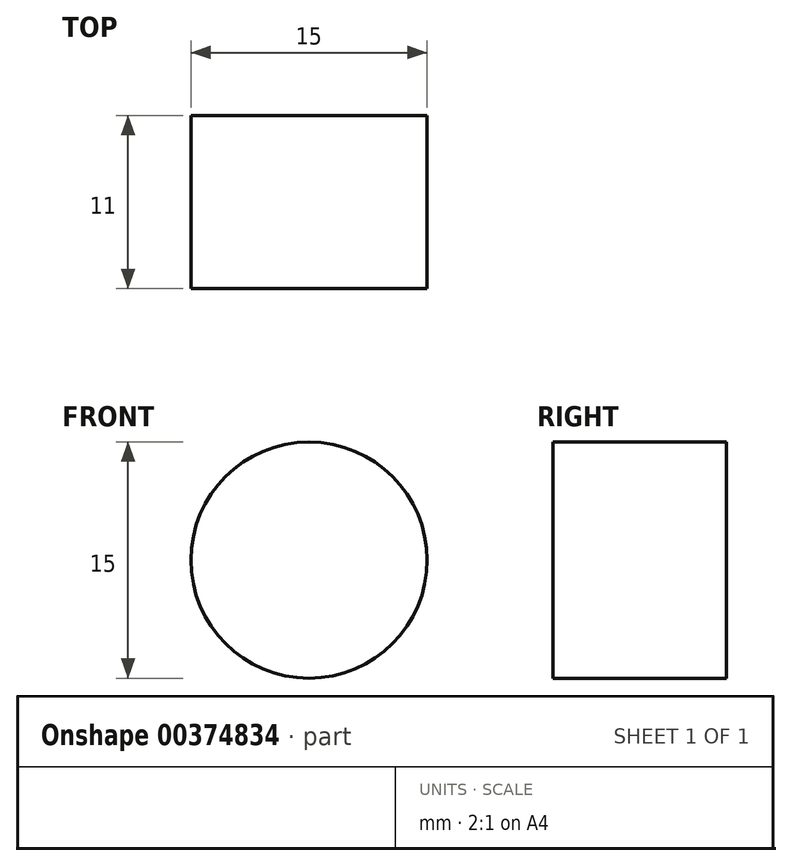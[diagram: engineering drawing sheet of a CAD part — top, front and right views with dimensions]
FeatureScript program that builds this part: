
annotation { "Feature Type Name" : "Feature", "Feature Type Description" : "" }
export const myFeature = defineFeature(function(context is Context, id is Id, definition is map)
    precondition{}
    {
        {
            var Q0;
            Q0=qCreatedBy(makeId("Front.planeOp"), FACE);
            var sketch = newSketch(context, id + "F0", { "sketchPlane" : qUnion([Q0])});
            skCircle(sketch, "E0", {"center": v(0, 0) * mm, "radius": 7.5 * mm});
            skSolve(sketch);
        }
        {
            var Q0;
            Q0 = qSketchRegion(id + "F0", true);
            extrude(context, id + "F1", {"entities" : qUnion([Q0]), "depth" : 11 * mm, "offsetDistance" : 25 * mm});
        }
    });
